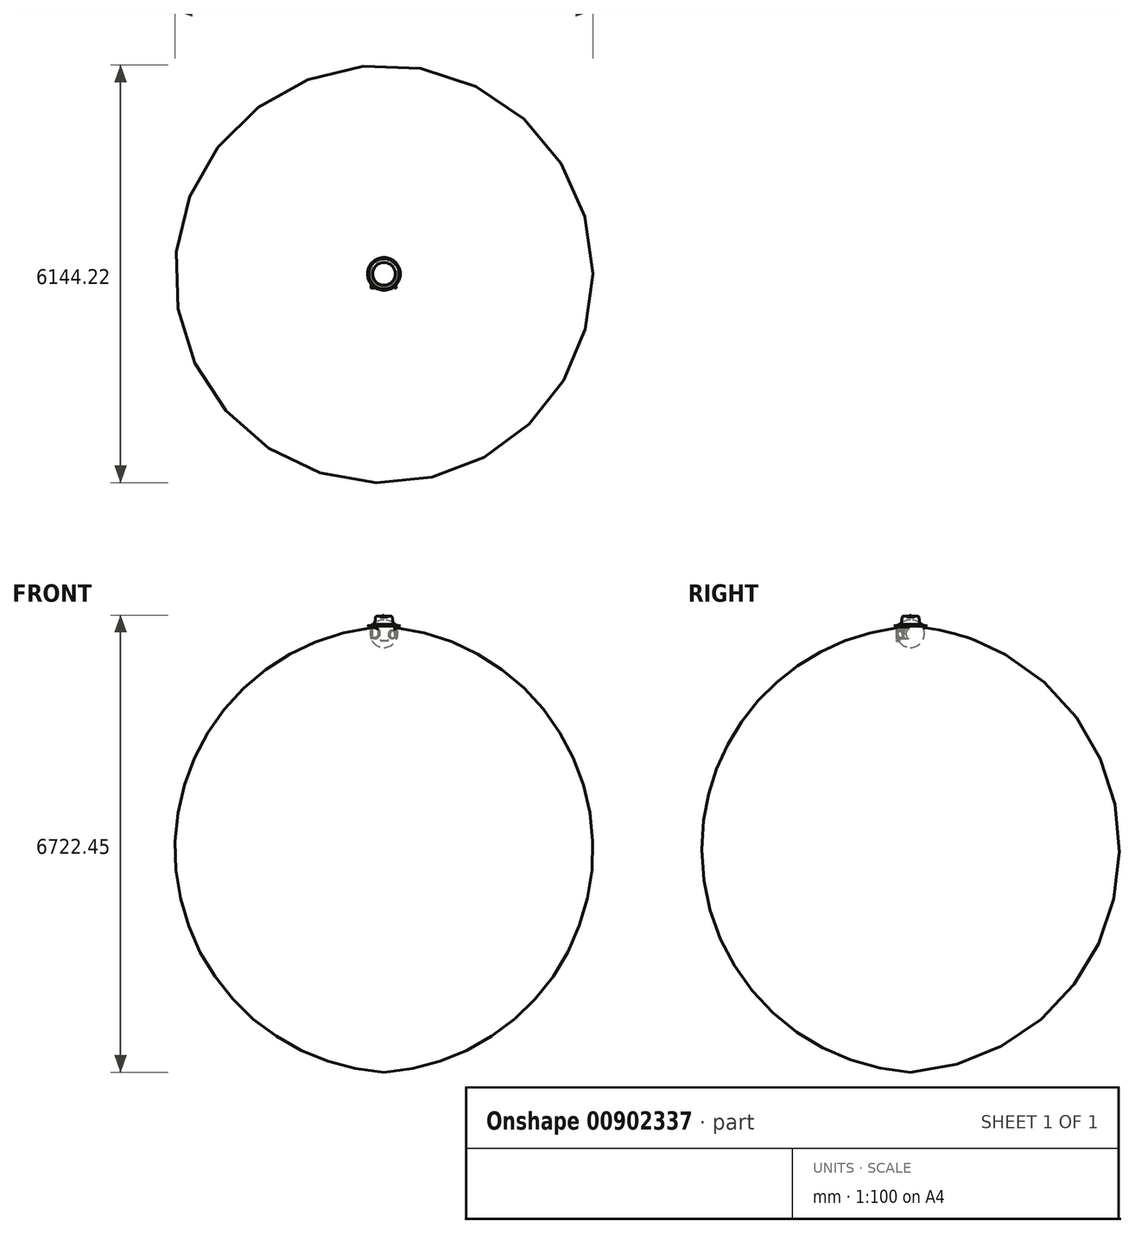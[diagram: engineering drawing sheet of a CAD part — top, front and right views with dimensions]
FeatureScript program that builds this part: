
annotation { "Feature Type Name" : "Feature", "Feature Type Description" : "" }
export const myFeature = defineFeature(function(context is Context, id is Id, definition is map)
    precondition{}
    {
        {
            var Q0;
            Q0=qCreatedBy(makeId("Front.planeOp"),FACE);
            var sketch = newSketch(context, id + "F0", { "sketchPlane" : qUnion([Q0])});
            skArc(sketch, "E0", {"start": v(0, 203.92) * mm, "mid": v(-203.92, 0) * mm, "end": v(0, -203.92) * mm});
            skLineSegment(sketch, "E1", {"start": v(0, 203.92) * mm, "end": v(0, -203.92) * mm});
            skSolve(sketch);
        }
        {
            var Q0;
            Q0=makeQuery(id+"F0.imprint","IMPRINT",FACE,{"disambiguationData":[TD([[makeQuery(id+"F0.imprint","IMPRINT",EDGE,{"derivedFrom":sQuery(id+"F0.wireOp",EDGE,"E0")}),1.0]])]});
            var Q1;
            Q1=sQuery(id+"F0.wireOp",EDGE,"E1");
            revolve(context, id + "F1", {"surfaceOperationType" : NewSurfaceOperationType.NEW, "entities" : qUnion([Q0]), "axis" : qUnion([Q1]), "revolveType" : RevolveType.FULL});
        }
        {
            var Q0;
            Q0=qCreatedBy(makeId("Front.planeOp"),FACE);
            var sketch = newSketch(context, id + "F2", { "sketchPlane" : qUnion([Q0])});
            skText(sketch, "E2", { "text": "D_d", "fontName": "OpenSans-Regular.ttf"});
            const initialGuessF2  = {"E2": [-0.21403, -0.07445, 1, 0, 0.166]};
            skSetInitialGuess(sketch, initialGuessF2);
            skSolve(sketch);
        }
        {
            var Q0;
            Q0 = qSketchRegion(id + "F2", true);
            var Q1;
            Q1=makeQuery(id+"F1.opRevolve","SWEPT_BODY",BODY,{"disambiguationData":[OSD([sQuery(id+"F0.wireOp",EDGE,"E0"),sQuery(id+"F0.wireOp",EDGE,"E1")])]});
            extrude(context, id + "F3", {"entities" : qUnion([Q0]), "operationType" : NewBodyOperationType.ADD, "depth" : 203.2 * mm, "hasOffset" : true, "offsetDistance" : 127 * mm, "hasSecondDirection" : true, "secondDirectionOppositeDirection" : false, "secondDirectionDepth" : 25.4 * mm, "secondDirectionBoundEntityBody" : qUnion([Q1])});
        }
        {
            var Q0;
            Q0=makeQuery(id+"F3.opExtrude","CAP_FACE",FACE,{"disambiguationData":[OSD([sQuery(id+"F2.wireOp",EDGE,"E2.sketch_text.stroke-0"),sQuery(id+"F2.wireOp",EDGE,"E2.sketch_text.stroke-1"),sQuery(id+"F2.wireOp",EDGE,"E2.sketch_text.stroke-2"),sQuery(id+"F2.wireOp",EDGE,"E2.sketch_text.stroke-3"),sQuery(id+"F2.wireOp",EDGE,"E2.sketch_text.stroke-4"),sQuery(id+"F2.wireOp",EDGE,"E2.sketch_text.stroke-5"),sQuery(id+"F2.wireOp",EDGE,"E2.sketch_text.stroke-6"),sQuery(id+"F2.wireOp",EDGE,"E2.sketch_text.stroke-7"),sQuery(id+"F2.wireOp",EDGE,"E2.sketch_text.stroke-8"),sQuery(id+"F2.wireOp",EDGE,"E2.sketch_text.stroke-9"),sQuery(id+"F2.wireOp",EDGE,"E2.sketch_text.stroke-10"),sQuery(id+"F2.wireOp",EDGE,"E2.sketch_text.stroke-11"),sQuery(id+"F2.wireOp",EDGE,"E2.sketch_text.stroke-12"),sQuery(id+"F2.wireOp",EDGE,"E2.sketch_text.stroke-13")])],"isStart":false});
            var Q1;
            Q1=makeQuery(id+"F3.opExtrude","CAP_FACE",FACE,{"disambiguationData":[OSD([sQuery(id+"F2.wireOp",EDGE,"E2.sketch_text.stroke-18"),sQuery(id+"F2.wireOp",EDGE,"E2.sketch_text.stroke-19"),sQuery(id+"F2.wireOp",EDGE,"E2.sketch_text.stroke-20"),sQuery(id+"F2.wireOp",EDGE,"E2.sketch_text.stroke-21"),sQuery(id+"F2.wireOp",EDGE,"E2.sketch_text.stroke-22"),sQuery(id+"F2.wireOp",EDGE,"E2.sketch_text.stroke-23"),sQuery(id+"F2.wireOp",EDGE,"E2.sketch_text.stroke-24"),sQuery(id+"F2.wireOp",EDGE,"E2.sketch_text.stroke-25"),sQuery(id+"F2.wireOp",EDGE,"E2.sketch_text.stroke-26"),sQuery(id+"F2.wireOp",EDGE,"E2.sketch_text.stroke-27"),sQuery(id+"F2.wireOp",EDGE,"E2.sketch_text.stroke-28"),sQuery(id+"F2.wireOp",EDGE,"E2.sketch_text.stroke-29"),sQuery(id+"F2.wireOp",EDGE,"E2.sketch_text.stroke-30"),sQuery(id+"F2.wireOp",EDGE,"E2.sketch_text.stroke-31"),sQuery(id+"F2.wireOp",EDGE,"E2.sketch_text.stroke-32"),sQuery(id+"F2.wireOp",EDGE,"E2.sketch_text.stroke-33"),sQuery(id+"F2.wireOp",EDGE,"E2.sketch_text.stroke-34"),sQuery(id+"F2.wireOp",EDGE,"E2.sketch_text.stroke-35"),sQuery(id+"F2.wireOp",EDGE,"E2.sketch_text.stroke-36"),sQuery(id+"F2.wireOp",EDGE,"E2.sketch_text.stroke-37"),sQuery(id+"F2.wireOp",EDGE,"E2.sketch_text.stroke-38"),sQuery(id+"F2.wireOp",EDGE,"E2.sketch_text.stroke-39"),sQuery(id+"F2.wireOp",EDGE,"E2.sketch_text.stroke-40"),sQuery(id+"F2.wireOp",EDGE,"E2.sketch_text.stroke-41")])],"isStart":false});
            var Q2;
            Q2=makeQuery(id+"F3.opExtrude","CAP_FACE",FACE,{"disambiguationData":[OSD([sQuery(id+"F2.wireOp",EDGE,"E2.sketch_text.stroke-14"),sQuery(id+"F2.wireOp",EDGE,"E2.sketch_text.stroke-15"),sQuery(id+"F2.wireOp",EDGE,"E2.sketch_text.stroke-16"),sQuery(id+"F2.wireOp",EDGE,"E2.sketch_text.stroke-17")])],"isStart":false});
            var Q3;
            {var subQ11=sQuery(id+"F2.wireOp",EDGE,"E2.sketch_text.stroke-0");Q3=makeQuery(id+"F3.boolean.opBoolean","SPLIT",FACE,{"disambiguationData":[TD([makeQuery(id+"F3.opExtrude","SWEPT_FACE",FACE,{"disambiguationData":[OSD([subQ11])]})])],"derivedFrom":makeQuery(id+"F1.opRevolve","SWEPT_FACE",FACE,{"disambiguationData":[OSD([sQuery(id+"F0.wireOp",EDGE,"E0")])]})});}
            extrude(context, id + "F4", {"entities" : qUnion([Q0, Q1, Q2]), "depth" : 5.08 * mm, "endBoundEntityFace" : qUnion([Q3]), "offsetDistance" : 25.4 * mm});
        }
        {
            var Q0;
            Q0=makeQuery(id+"F4.opExtrude","CAP_EDGE",EDGE,{"disambiguationData":[OSD([sQuery(id+"F2.wireOp",EDGE,"E2.sketch_text.stroke-12")])],"isStart":false});
            var Q1;
            Q1=makeQuery(id+"F4.opExtrude","CAP_EDGE",EDGE,{"disambiguationData":[OSD([sQuery(id+"F2.wireOp",EDGE,"E2.sketch_text.stroke-3")])],"isStart":false});
            var Q2;
            Q2=makeQuery(id+"F4.opExtrude","CAP_EDGE",EDGE,{"disambiguationData":[OSD([sQuery(id+"F2.wireOp",EDGE,"E2.sketch_text.stroke-2")])],"isStart":false});
            var Q3;
            Q3=makeQuery(id+"F4.opExtrude","CAP_EDGE",EDGE,{"disambiguationData":[OSD([sQuery(id+"F2.wireOp",EDGE,"E2.sketch_text.stroke-10")])],"isStart":false});
            var Q4;
            Q4=makeQuery(id+"F4.opExtrude","CAP_EDGE",EDGE,{"disambiguationData":[OSD([sQuery(id+"F2.wireOp",EDGE,"E2.sketch_text.stroke-14")])],"isStart":false});
            var Q5;
            Q5=makeQuery(id+"F3.boolean.opBoolean","INTERSECT",EDGE,{"derivedFrom":[makeQuery(id+"F1.opRevolve","SWEPT_FACE",FACE,{"disambiguationData":[OSD([sQuery(id+"F0.wireOp",EDGE,"E0")])]}),makeQuery(id+"F3.opExtrude","SWEPT_FACE",FACE,{"disambiguationData":[OSD([sQuery(id+"F2.wireOp",EDGE,"E2.sketch_text.stroke-16")])]})]});
            var Q6;
            Q6=makeQuery(id+"F4.opExtrude","CAP_FACE",FACE,{"disambiguationData":[OSD([sQuery(id+"F2.wireOp",EDGE,"E2.sketch_text.stroke-14"),sQuery(id+"F2.wireOp",EDGE,"E2.sketch_text.stroke-15"),sQuery(id+"F2.wireOp",EDGE,"E2.sketch_text.stroke-16"),sQuery(id+"F2.wireOp",EDGE,"E2.sketch_text.stroke-17")])],"isStart":false});
            var Q7;
            Q7=makeQuery(id+"F4.opExtrude","CAP_FACE",FACE,{"disambiguationData":[OSD([sQuery(id+"F2.wireOp",EDGE,"E2.sketch_text.stroke-18"),sQuery(id+"F2.wireOp",EDGE,"E2.sketch_text.stroke-19"),sQuery(id+"F2.wireOp",EDGE,"E2.sketch_text.stroke-20"),sQuery(id+"F2.wireOp",EDGE,"E2.sketch_text.stroke-21"),sQuery(id+"F2.wireOp",EDGE,"E2.sketch_text.stroke-22"),sQuery(id+"F2.wireOp",EDGE,"E2.sketch_text.stroke-23"),sQuery(id+"F2.wireOp",EDGE,"E2.sketch_text.stroke-24"),sQuery(id+"F2.wireOp",EDGE,"E2.sketch_text.stroke-25"),sQuery(id+"F2.wireOp",EDGE,"E2.sketch_text.stroke-26"),sQuery(id+"F2.wireOp",EDGE,"E2.sketch_text.stroke-27"),sQuery(id+"F2.wireOp",EDGE,"E2.sketch_text.stroke-28"),sQuery(id+"F2.wireOp",EDGE,"E2.sketch_text.stroke-29"),sQuery(id+"F2.wireOp",EDGE,"E2.sketch_text.stroke-30"),sQuery(id+"F2.wireOp",EDGE,"E2.sketch_text.stroke-31"),sQuery(id+"F2.wireOp",EDGE,"E2.sketch_text.stroke-32"),sQuery(id+"F2.wireOp",EDGE,"E2.sketch_text.stroke-33"),sQuery(id+"F2.wireOp",EDGE,"E2.sketch_text.stroke-34"),sQuery(id+"F2.wireOp",EDGE,"E2.sketch_text.stroke-35"),sQuery(id+"F2.wireOp",EDGE,"E2.sketch_text.stroke-36"),sQuery(id+"F2.wireOp",EDGE,"E2.sketch_text.stroke-37"),sQuery(id+"F2.wireOp",EDGE,"E2.sketch_text.stroke-38"),sQuery(id+"F2.wireOp",EDGE,"E2.sketch_text.stroke-39"),sQuery(id+"F2.wireOp",EDGE,"E2.sketch_text.stroke-40"),sQuery(id+"F2.wireOp",EDGE,"E2.sketch_text.stroke-41")])],"isStart":false});
            fillet(context, id + "F5", {"entities" : qUnion([Q0, Q1, Q2, Q3, Q4, Q5, Q6, Q7]), "radius" : 5.08 * mm, "tangentPropagation" : true, "rho" : 0.5, "crossSection" : FilletCrossSection.CONIC, "allowEdgeOverflow" : false});
        }
        {
            var Q0;
            Q0=qCreatedBy(makeId("Front.planeOp"),FACE);
            var sketch = newSketch(context, id + "F6", { "sketchPlane" : qUnion([Q0])});
            skLineSegment(sketch, "E3", {"start": v(0, 106.62) * mm, "end": v(0, 269.82) * mm});
            skFitSpline(sketch, "E4", {"points": [v(0, 269.82) * mm, v(-48.96, 247.1) * mm, v(-115.13, 254.84) * mm, v(-144.23, 154.15) * mm, v(-302.27, 128.08) * mm, v(-348.45, 124.05) * mm, v(-348.04, 110.86) * mm, v(0, 106.62) * mm, v(0, 269.82) * mm]});
            skArc(sketch, "E5", {"start": v(0, 106.62) * mm, "mid": v(-120.94, 112.28) * mm, "end": v(-242, 113.48) * mm});
            skLineSegment(sketch, "E6", {"start": v(0, 154.15) * mm, "end": v(0, 137.26) * mm});
            skPoint(sketch, "E7", {"position": v(-188.89, 120.45) * mm});
            skPoint(sketch, "E8", {"position": v(-232.86, 125.39) * mm});
            skPoint(sketch, "E9", {"position": v(-242, 113.48) * mm});
            skPoint(sketch, "E10", {"position": v(-224.77, 117.8) * mm});
            skArc(sketch, "E11", {"start": v(-224.77, 117.8) * mm, "mid": v(-194.22, 122.8) * mm, "end": v(-166.87, 137.26) * mm});
            skLineSegment(sketch, "E12", {"start": v(-224.77, 117.8) * mm, "end": v(-242, 113.48) * mm});
            skPoint(sketch, "E13.1.internal.snap0", {"position": v(-233.38, 115.64) * mm});
            skFitSpline(sketch, "E13", {"points": [v(-224.77, 117.8) * mm, v(-283.74, 115.64) * mm, v(-224.77, 113.48) * mm, v(-194.22, 122.8) * mm, v(-224.77, 117.8) * mm]});
            skSolve(sketch);
        }
        {
            var Q0;
            {var subQ0=sQuery(id+"F6.wireOp",EDGE,"E3");Q0=makeQuery(id+"F6.imprint","IMPRINT",FACE,{"disambiguationData":[TD([[makeQuery(id+"F6.imprint","IMPRINT",EDGE,{"derivedFrom":subQ0}),1.0]])]});}
            var Q1;
            {var subQ0=sQuery(id+"F6.wireOp",EDGE,"8a0e3727-b197-491a-9d34-e035e25ed180");Q1=makeQuery(id+"F6.imprint","IMPRINT",FACE,{"disambiguationData":[TD([[makeQuery(id+"F6.imprint","IMPRINT",EDGE,{"derivedFrom":subQ0}),-1.0]])]});}
            var Q2;
            {var subQ1=sQuery(id+"F6.wireOp",EDGE,"E5");Q2=makeQuery(id+"F6.imprint","IMPRINT",FACE,{"disambiguationData":[TD([[makeQuery(id+"F6.imprint","IMPRINT",EDGE,{"derivedFrom":subQ1}),-1.0]])]});}
            var Q3;
            Q3=sQuery(id+"F6.wireOp",EDGE,"E3");
            revolve(context, id + "F7", {"surfaceOperationType" : NewSurfaceOperationType.NEW, "entities" : qUnion([Q0, Q1, Q2]), "axis" : qUnion([Q3]), "revolveType" : RevolveType.FULL});
        }
    });
